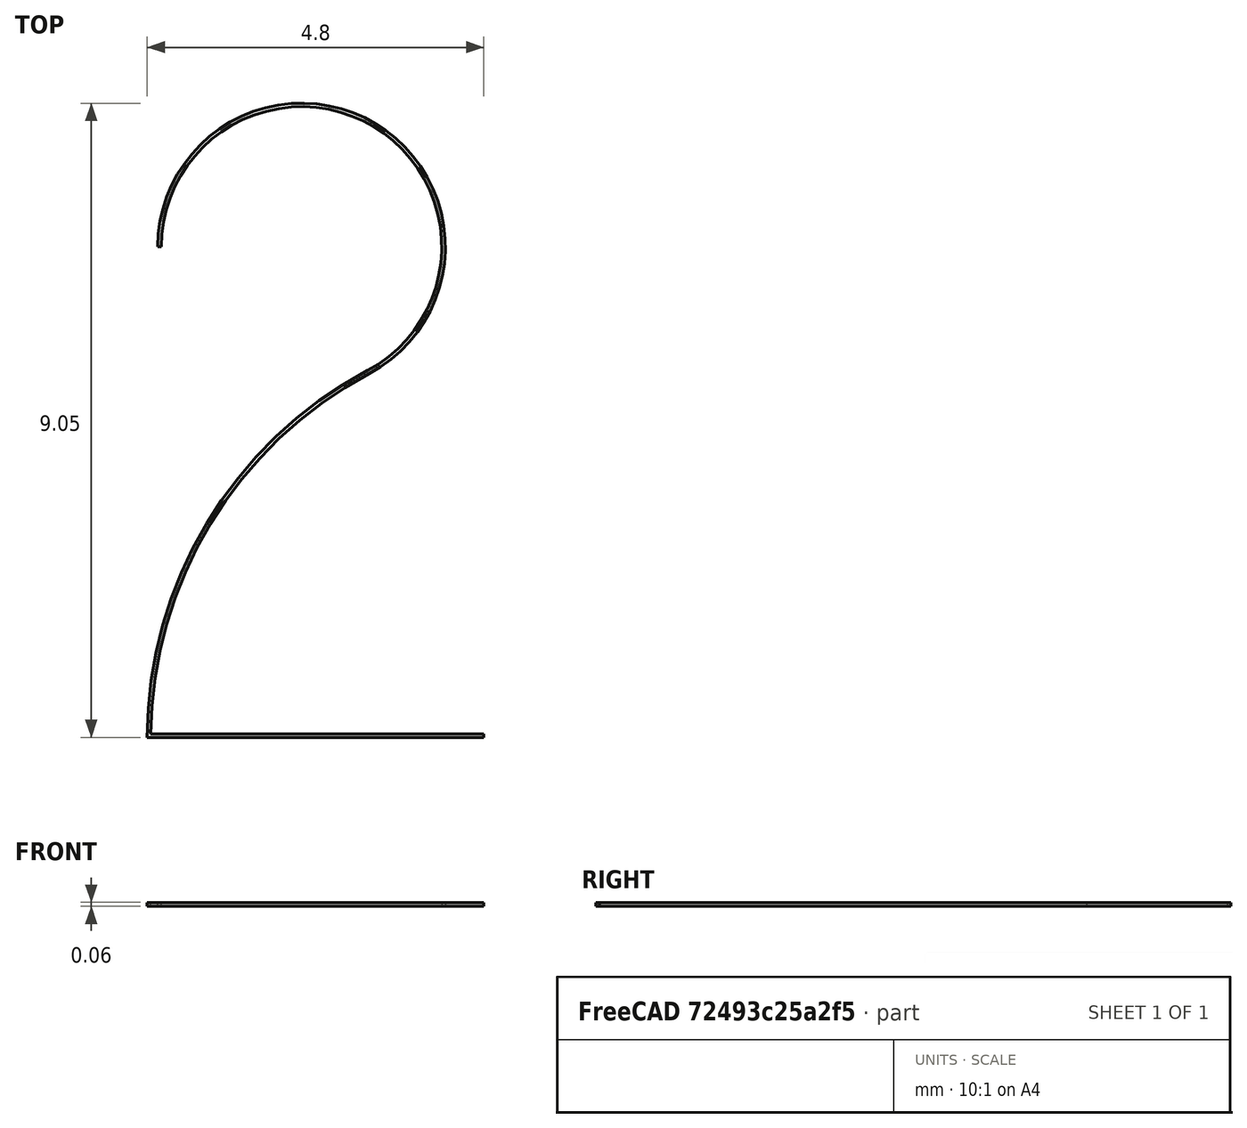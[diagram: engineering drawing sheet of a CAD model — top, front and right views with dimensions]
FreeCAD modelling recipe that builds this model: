
FCSTD DOCUMENT  (FreeCAD 0.16R6712 (Git))
Label: 2t
License: All rights reserved
LicenseURL: http://en.wikipedia.org/wiki/All_rights_reserved
objects: Sketcher::SketchObject×1, PartDesign::Pad×1, Mesh::Feature×1
note: 3 computed .brp shape members not serialized (recipe doc carries the construction recipe); baked Part::Feature solids carry a one-line shape summary decoded from their .brp

FEATURE [Sketcher::SketchObject] Sketch
  sketch-geometry (8):
    g0: ArcOfCircle CenterX=0 CenterY=7 CenterZ=0 NormalX=0 NormalY=0 NormalZ=1 Radius=2 StartAngle=5.20235 EndAngle=9.42478
    g1: LineSegment StartX=-2.2 StartY=0 StartZ=0 EndX=2.6 EndY=0 EndZ=0
    g2: ArcOfCircle CenterX=3.73333 CenterY=0 CenterZ=0 NormalX=0 NormalY=0 NormalZ=1 Radius=5.93333 StartAngle=2.06075 EndAngle=3.14159
    g3: ArcOfCircle CenterX=0 CenterY=7 CenterZ=0 NormalX=0 NormalY=0 NormalZ=1 Radius=2.05 StartAngle=5.20235 EndAngle=9.42478
    g4: LineSegment StartX=2.6 StartY=0.05 StartZ=0 EndX=-2.14979 EndY=0.05 EndZ=0
    g5: LineSegment StartX=-2.05 StartY=7 StartZ=0 EndX=-2 EndY=7 EndZ=0
    g6: LineSegment StartX=2.6 StartY=0 StartZ=0 EndX=2.6 EndY=0.05 EndZ=0
    g7: ArcOfCircle CenterX=3.73333 CenterY=0 CenterZ=0 NormalX=0 NormalY=0 NormalZ=1 Radius=5.88333 StartAngle=2.06075 EndAngle=3.13309
  constraints (27):
    c: PointOnObject(g0,g-2)
    c: PointOnObject(g1,g-1)
    c: PointOnObject(g1,g-1)
    c: Coincident(g2,g1)
    c: Radius(g0) = 2
    c: Coincident(g2,g0)
    c: DistanceY(g-1,g0) = 7
    c: Tangent(g0,g2)
    c: DistanceX(g-2,g1) = -2.2
    c: Distance(g-1,g1) = 2.6
    c: DistanceY(g1,g0) = 7
    c: Coincident(g3,g0)
    c: Horizontal(g4)
    c: DistanceY(g-1,g3) = 7
    c: Coincident(g5,g3)
    c: Coincident(g5,g0)
    c: Coincident(g6,g1)
    c: Coincident(g6,g4)
    c: Vertical(g6)
    c: DistanceX(g3,g0) = 0.05
    c: DistanceY(g-1,g4) = 0.05
    c: Perpendicular(g2,g1)
    c: Coincident(g7,g2)
    c: Coincident(g7,g3)
    c: PointOnObject(g7,g4)
    c: Coincident(g4,g7)
    c: Tangent(g3,g7)
FEATURE [PartDesign::Pad] Pad
  Length = 0.05
  Length2 = 100
  Midplane = true
  Sketch = -> Sketch
  Type = 0
FEATURE [Mesh::Feature] Mesh  label="Pad (Meshed)"
